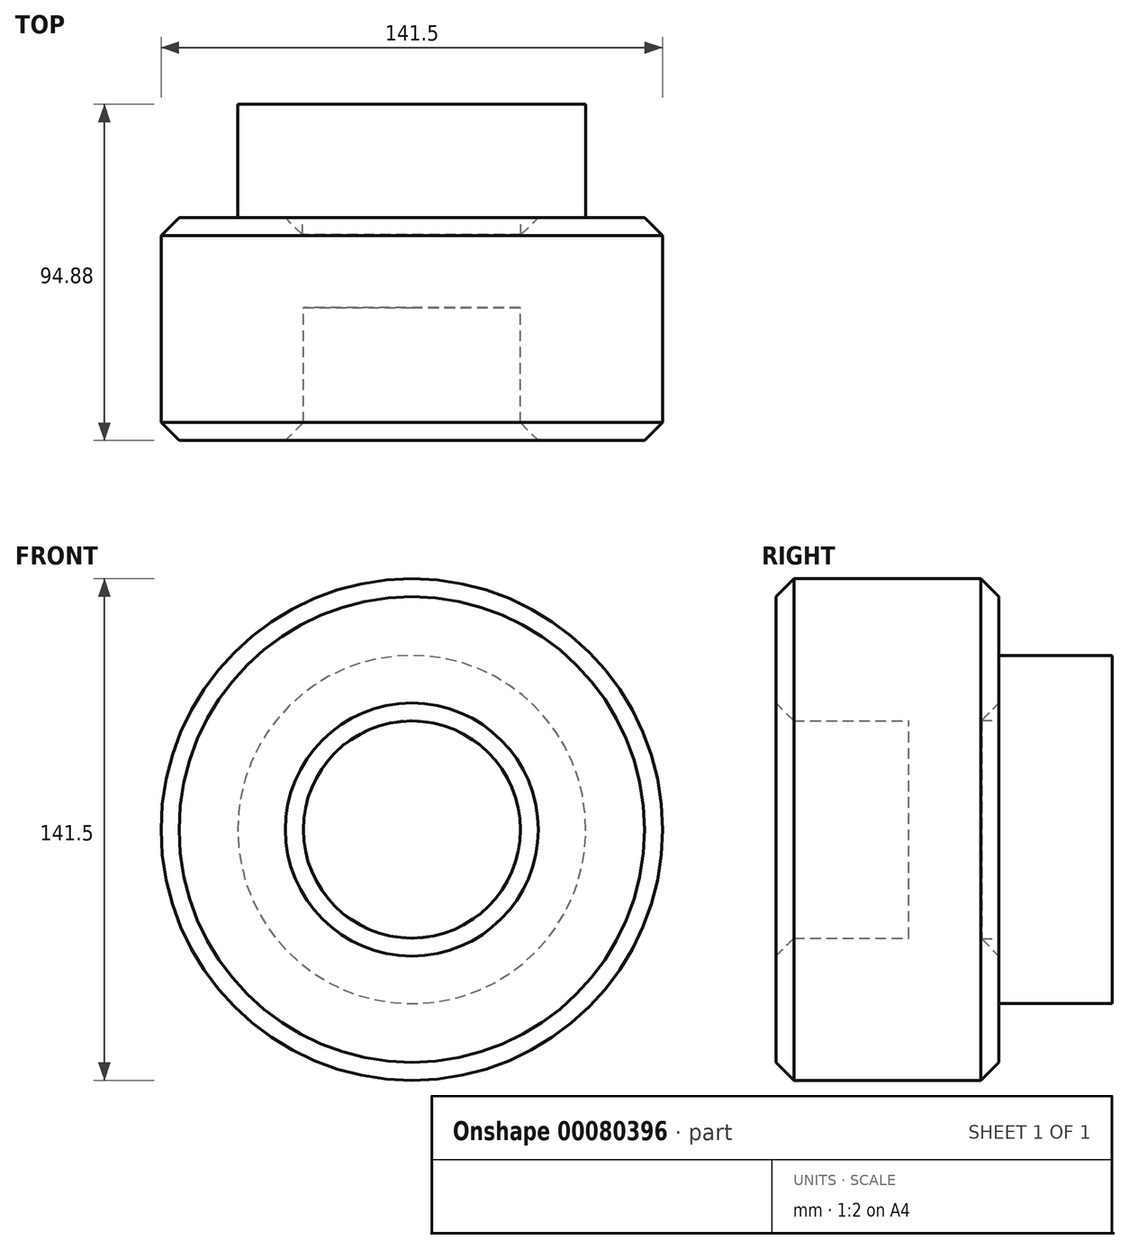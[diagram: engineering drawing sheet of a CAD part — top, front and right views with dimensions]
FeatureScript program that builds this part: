
annotation { "Feature Type Name" : "Feature", "Feature Type Description" : "" }
export const myFeature = defineFeature(function(context is Context, id is Id, definition is map)
    precondition{}
    {
        {
            var Q0;
            Q0=qCreatedBy(makeId("Front.planeOp"),FACE);
            var sketch = newSketch(context, id + "F0", { "sketchPlane" : qUnion([Q0])});
            skCircle(sketch, "E0", {"center": v(0, 0) * mm, "radius": 70.75 * mm});
            skCircle(sketch, "E1", {"center": v(0, 0) * mm, "radius": 30.62 * mm});
            skSolve(sketch);
        }
        {
            var Q0;
            Q0 = qSketchRegion(id + "F0", true);
            extrude(context, id + "F1", {"entities" : qUnion([Q0]), "depth" : 62.94 * mm});
        }
        {
            var Q0;
            Q0=makeQuery(id+"F1.opExtrude","CAP_EDGE",EDGE,{"disambiguationData":[OSD([sQuery(id+"F0.wireOp",EDGE,"E0")])],"isStart":false});
            var Q1;
            Q1=makeQuery(id+"F1.opExtrude","CAP_EDGE",EDGE,{"disambiguationData":[OSD([sQuery(id+"F0.wireOp",EDGE,"E1")])],"isStart":false});
            var Q2;
            Q2=makeQuery(id+"F1.opExtrude","CAP_EDGE",EDGE,{"disambiguationData":[OSD([sQuery(id+"F0.wireOp",EDGE,"E0")])],"isStart":true});
            var Q3;
            Q3=makeQuery(id+"F1.opExtrude","CAP_EDGE",EDGE,{"disambiguationData":[OSD([sQuery(id+"F0.wireOp",EDGE,"E1")])],"isStart":true});
            chamfer(context, id + "F2", {"entities" : qUnion([Q0, Q1, Q2, Q3]), "width" : 5.08 * mm, "tangentPropagation" : true});
        }
        {
            var Q0;
            Q0=makeQuery(id+"F1.opExtrude","CAP_FACE",FACE,{"disambiguationData":[OSD([sQuery(id+"F0.wireOp",EDGE,"E0"),sQuery(id+"F0.wireOp",EDGE,"E1")])],"isStart":true});
            var sketch = newSketch(context, id + "F3", { "sketchPlane" : qUnion([Q0])});
            skCircle(sketch, "E2", {"center": v(0, 0) * mm, "radius": 49.11 * mm});
            skSolve(sketch);
        }
        {
            var Q0;
            Q0 = qSketchRegion(id + "F3", true);
            extrude(context, id + "F4", {"entities" : qUnion([Q0]), "operationType" : NewBodyOperationType.ADD, "depth" : 31.94 * mm});
        }
        {
            var Q0;
            Q0=qCreatedBy(makeId("Front.planeOp"),FACE);
            var sketch = newSketch(context, id + "F5", { "sketchPlane" : qUnion([Q0])});
            skCircle(sketch, "E3", {"center": v(0, 0) * mm, "radius": 30.8 * mm});
            skSolve(sketch);
        }
        {
            var Q0;
            Q0 = qSketchRegion(id + "F5", true);
            extrude(context, id + "F6", {"entities" : qUnion([Q0]), "operationType" : NewBodyOperationType.ADD, "depth" : 25.4 * mm});
        }
    });
